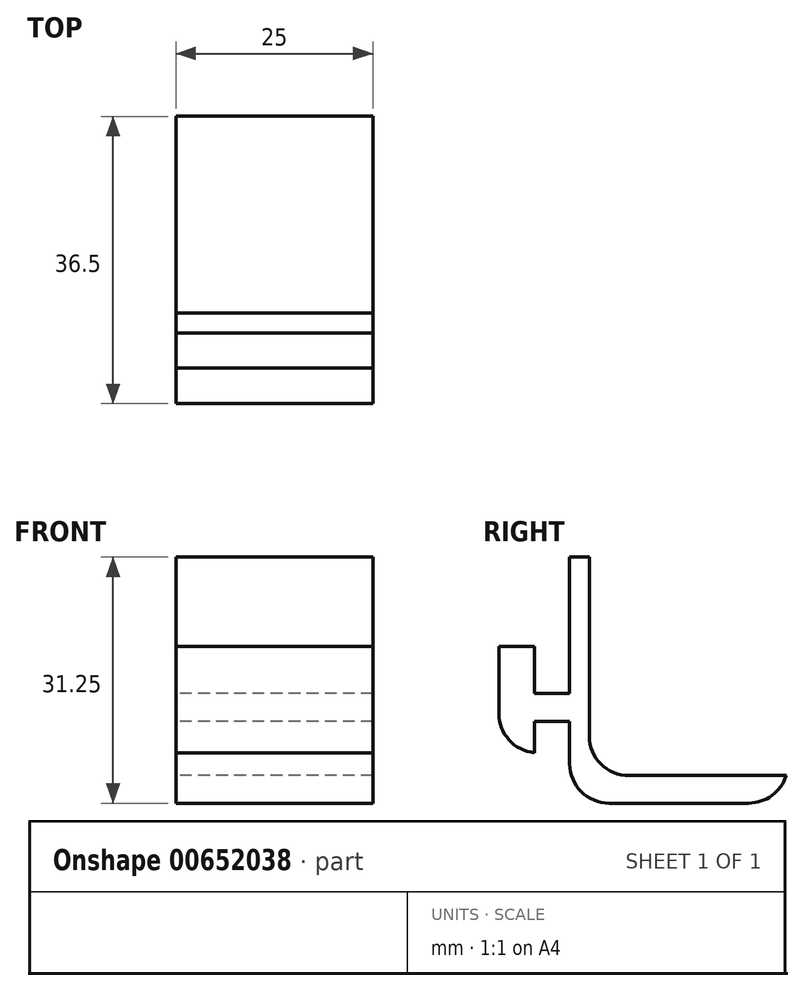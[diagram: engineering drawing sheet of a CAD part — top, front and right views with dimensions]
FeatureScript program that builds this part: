
annotation { "Feature Type Name" : "Feature", "Feature Type Description" : "" }
export const myFeature = defineFeature(function(context is Context, id is Id, definition is map)
    precondition{}
    {
        {
            var Q0;
            Q0=qCreatedBy(makeId("Right.planeOp"),FACE);
            var sketch = newSketch(context, id + "F0", { "sketchPlane" : qUnion([Q0])});
            skLineSegment(sketch, "E0", {"start": v(0.05, 4.64) * mm, "end": v(0.05, -8.86) * mm});
            skLineSegment(sketch, "E1", {"start": v(0.05, -8.86) * mm, "end": v(4.55, -8.86) * mm});
            skLineSegment(sketch, "E2", {"start": v(4.55, -8.86) * mm, "end": v(4.55, -4.86) * mm});
            skLineSegment(sketch, "E3", {"start": v(4.55, -4.86) * mm, "end": v(9.05, -4.86) * mm});
            skLineSegment(sketch, "E4", {"start": v(9.05, -4.86) * mm, "end": v(9.05, -15.28) * mm});
            skLineSegment(sketch, "E5", {"start": v(9.05, -15.28) * mm, "end": v(11.55, -15.28) * mm});
            skLineSegment(sketch, "E6", {"start": v(11.55, -15.28) * mm, "end": v(11.55, 15.97) * mm});
            skLineSegment(sketch, "E7", {"start": v(11.55, 15.97) * mm, "end": v(9.05, 15.97) * mm});
            skLineSegment(sketch, "E8", {"start": v(9.05, 15.97) * mm, "end": v(9.05, -1.36) * mm});
            skLineSegment(sketch, "E9", {"start": v(9.05, -1.36) * mm, "end": v(4.55, -1.36) * mm});
            skLineSegment(sketch, "E10", {"start": v(4.55, -1.36) * mm, "end": v(4.55, 4.64) * mm});
            skLineSegment(sketch, "E11", {"start": v(4.55, 4.64) * mm, "end": v(0.05, 4.64) * mm});
            skLineSegment(sketch, "E12.bottom", {"start": v(11.55, -15.28) * mm, "end": v(36.55, -15.28) * mm});
            skLineSegment(sketch, "E12.top", {"start": v(11.55, -11.78) * mm, "end": v(36.55, -11.78) * mm});
            skLineSegment(sketch, "E12.left", {"start": v(11.55, -15.28) * mm, "end": v(11.55, -11.78) * mm});
            skLineSegment(sketch, "E12.right", {"start": v(36.55, -15.28) * mm, "end": v(36.55, -11.78) * mm});
            skLineSegment(sketch, "E13.bottom", {"start": v(36.55, -11.78) * mm, "end": v(34.05, -11.78) * mm});
            skLineSegment(sketch, "E13.top", {"start": v(36.55, -7.91) * mm, "end": v(34.05, -7.91) * mm});
            skLineSegment(sketch, "E13.left", {"start": v(36.55, -11.78) * mm, "end": v(36.55, -7.91) * mm});
            skLineSegment(sketch, "E13.right", {"start": v(34.05, -11.78) * mm, "end": v(34.05, -7.91) * mm});
            skSolve(sketch);
        }
        {
            var Q0;
            Q0=makeQuery(id+"F0.imprint","IMPRINT",FACE,{"disambiguationData":[TD([[makeQuery(id+"F0.imprint","IMPRINT",EDGE,{"derivedFrom":sQuery(id+"F0.wireOp",EDGE,"E0")}),1.0]])]});
            var Q1;
            Q1=makeQuery(id+"F0.imprint","IMPRINT",FACE,{"disambiguationData":[TD([[makeQuery(id+"F0.imprint","IMPRINT",EDGE,{"derivedFrom":sQuery(id+"F0.wireOp",EDGE,"E12.bottom")}),1.0]])]});
            var Q2;
            Q2=makeQuery(id+"F0.imprint","IMPRINT",FACE,{"disambiguationData":[TD([[makeQuery(id+"F0.imprint","IMPRINT",EDGE,{"derivedFrom":sQuery(id+"F0.wireOp",EDGE,"E13.bottom")}),-1.0]])]});
            extrude(context, id + "F1", {"entities" : qUnion([Q0, Q1, Q2]), "depth" : 25 * mm, "offsetDistance" : 25 * mm});
        }
        {
            var Q0;
            Q0=makeQuery(id+"F1.opExtrude","SWEPT_EDGE",EDGE,{"disambiguationData":[OSD([sQuery(id+"F0.wireOp",EDGE,"E6"),sQuery(id+"F0.wireOp",EDGE,"E12.top"),sQuery(id+"F0.wireOp",EDGE,"E12.left")])]});
            var Q1;
            Q1=makeQuery(id+"F1.opExtrude","SWEPT_EDGE",EDGE,{"disambiguationData":[OSD([sQuery(id+"F0.wireOp",EDGE,"E12.top"),sQuery(id+"F0.wireOp",EDGE,"E13.bottom"),sQuery(id+"F0.wireOp",EDGE,"E13.right")])]});
            var Q2;
            Q2=makeQuery(id+"F1.opExtrude","SWEPT_EDGE",EDGE,{"disambiguationData":[OSD([sQuery(id+"F0.wireOp",EDGE,"E12.bottom"),sQuery(id+"F0.wireOp",EDGE,"E12.right")])]});
            var Q3;
            Q3=makeQuery(id+"F1.opExtrude","SWEPT_EDGE",EDGE,{"disambiguationData":[OSD([sQuery(id+"F0.wireOp",EDGE,"E4"),sQuery(id+"F0.wireOp",EDGE,"E5")])]});
            fillet(context, id + "F2", {"entities" : qUnion([Q0, Q1, Q2, Q3]), "radius" : 5 * mm, "tangentPropagation" : true, "allowEdgeOverflow" : false});
        }
        {
            var Q0;
            Q0=makeQuery(id+"F1.opExtrude","SWEPT_EDGE",EDGE,{"disambiguationData":[OSD([sQuery(id+"F0.wireOp",EDGE,"E0"),sQuery(id+"F0.wireOp",EDGE,"E1")])]});
            fillet(context, id + "F3", {"entities" : qUnion([Q0]), "radius" : 5 * mm, "tangentPropagation" : true, "allowEdgeOverflow" : false});
        }
    });
